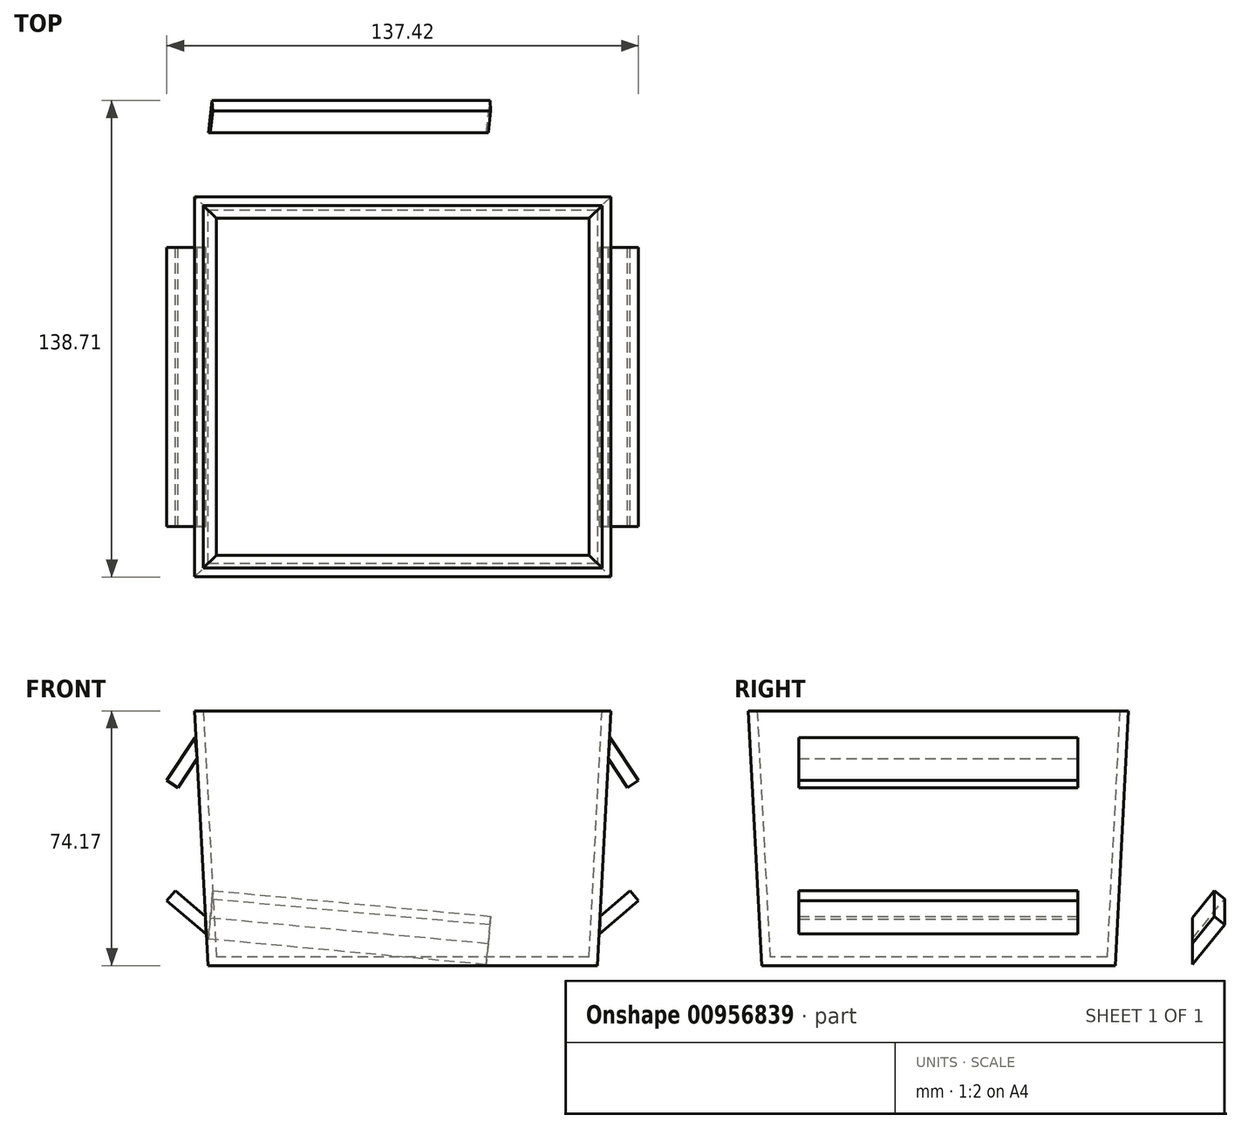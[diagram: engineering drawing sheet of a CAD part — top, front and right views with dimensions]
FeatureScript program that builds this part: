
annotation { "Feature Type Name" : "Feature", "Feature Type Description" : "" }
export const myFeature = defineFeature(function(context is Context, id is Id, definition is map)
    precondition{}
    {
        {
            var Q0;
            Q0=qCreatedBy(makeId("Top.planeOp"),FACE);
            var sketch = newSketch(context, id + "F0", { "sketchPlane" : qUnion([Q0])});
            skLineSegment(sketch, "E0.bottom", {"start": v(56.73, -51.48) * mm, "end": v(-56.73, -51.48) * mm});
            skLineSegment(sketch, "E0.top", {"start": v(56.73, 51.48) * mm, "end": v(-56.73, 51.48) * mm});
            skLineSegment(sketch, "E0.left", {"start": v(56.73, -51.48) * mm, "end": v(56.73, 51.48) * mm});
            skLineSegment(sketch, "E0.right", {"start": v(-56.73, -51.48) * mm, "end": v(-56.73, 51.48) * mm});
            skPoint(sketch, "E0.middle", {"position": v(0, 0) * mm});
            skSolve(sketch);
        }
        {
            var Q0;
            Q0 = qSketchRegion(id + "F0", true);
            extrude(context, id + "F1", {"entities" : qUnion([Q0]), "depth" : 74.17 * mm, "offsetDistance" : 25.4 * mm, "hasDraft" : true, "draftAngle" : 3 * degree});
        }
        {
            var Q0;
            Q0=makeQuery(id+"F1.opExtrude","CAP_FACE",FACE,{"disambiguationData":[OSD([sQuery(id+"F0.wireOp",EDGE,"E0.bottom"),sQuery(id+"F0.wireOp",EDGE,"E0.top"),sQuery(id+"F0.wireOp",EDGE,"E0.left"),sQuery(id+"F0.wireOp",EDGE,"E0.right")])],"isStart":false});
            shell(context, id + "F2", {"entities" : qUnion([Q0]), "thickness" : 2.54 * mm});
        }
        {
            var Q0;
            Q0=qCreatedBy(makeId("Front.planeOp"),FACE);
            var sketch = newSketch(context, id + "F3", { "sketchPlane" : qUnion([Q0])});
            skLineSegment(sketch, "E1", {"start": v(60.46, 66.31) * mm, "end": v(68.7, 53.89) * mm});
            skLineSegment(sketch, "E2", {"start": v(68.7, 53.89) * mm, "end": v(65.52, 51.77) * mm});
            skLineSegment(sketch, "E3", {"start": v(65.52, 51.77) * mm, "end": v(59.9, 60.23) * mm});
            skLineSegment(sketch, "E4", {"start": v(59.9, 60.23) * mm, "end": v(60.46, 66.31) * mm});
            skLineSegment(sketch, "E5", {"start": v(57.37, 9.22) * mm, "end": v(68.7, 18.93) * mm});
            skLineSegment(sketch, "E6", {"start": v(68.7, 18.93) * mm, "end": v(66.2, 21.84) * mm});
            skLineSegment(sketch, "E7", {"start": v(66.2, 21.84) * mm, "end": v(57.44, 14.33) * mm});
            skLineSegment(sketch, "E8", {"start": v(57.44, 14.33) * mm, "end": v(57.37, 9.22) * mm});
            skLineSegment(sketch, "E9", {"start": v(58.59, 37.27) * mm, "end": v(98.17, 35.2) * mm, "construction": true});
            skSolve(sketch);
        }
        {
            var Q0;
            Q0 = qSketchRegion(id + "F3", true);
            extrude(context, id + "F4", {"entities" : qUnion([Q0]), "operationType" : NewBodyOperationType.ADD, "endBound" : BoundingType.SYMMETRIC, "depth" : 81.28 * mm, "offsetDistance" : 25.4 * mm});
        }
        {
            var Q0;
            Q0=makeQuery(id+"F4.opExtrude","SWEPT_BODY",BODY,{"disambiguationData":[OSD([sQuery(id+"F3.wireOp",EDGE,"E1"),sQuery(id+"F3.wireOp",EDGE,"E2"),sQuery(id+"F3.wireOp",EDGE,"E3"),sQuery(id+"F3.wireOp",EDGE,"E4")])]});
            var Q1;
            Q1=makeQuery(id+"F1.opExtrude","SWEPT_BODY",BODY,{"disambiguationData":[OSD([sQuery(id+"F0.wireOp",EDGE,"E0.bottom"),sQuery(id+"F0.wireOp",EDGE,"E0.top"),sQuery(id+"F0.wireOp",EDGE,"E0.left"),sQuery(id+"F0.wireOp",EDGE,"E0.right")])]});
            var Q2;
            Q2=qCreatedBy(makeId("Right.planeOp"),FACE);
            mirror(context, id + "F5", {"operationType" : NewBodyOperationType.ADD, "entities" : qUnion([Q0, Q1]), "mirrorPlane" : qUnion([Q2])});
        }
        {
            var Q0;
            Q0=makeQuery(id+"F4.opExtrude","SWEPT_BODY",BODY,{"disambiguationData":[OSD([sQuery(id+"F3.wireOp",EDGE,"E1"),sQuery(id+"F3.wireOp",EDGE,"E2"),sQuery(id+"F3.wireOp",EDGE,"E3"),sQuery(id+"F3.wireOp",EDGE,"E4")])]});
            var Q1;
            Q1=makeQuery(id+"F1.opExtrude","CAP_EDGE",EDGE,{"disambiguationData":[OSD([sQuery(id+"F0.wireOp",EDGE,"E0.left")])],"isStart":false});
            transform(context, id + "F6", {"entities" : qUnion([Q0]), "transformType" : TransformType.TRANSLATION_ENTITY, "oppositeDirectionEntity" : false, "transformLine" : qUnion([Q1]), "makeCopy" : true});
        }
        {
            var Q0;
            Q0=makeQuery(id+"F6.opPattern","COPY",BODY,{"derivedFrom":makeQuery(id+"F4.opExtrude","SWEPT_BODY",BODY,{"disambiguationData":[OSD([sQuery(id+"F3.wireOp",EDGE,"E1"),sQuery(id+"F3.wireOp",EDGE,"E2"),sQuery(id+"F3.wireOp",EDGE,"E3"),sQuery(id+"F3.wireOp",EDGE,"E4")])]}),"instanceName":"1"});
            var Q1;
            Q1=makeQuery(id+"F6.opPattern","COPY",EDGE,{"derivedFrom":makeQuery(id+"F4.opExtrude","CAP_EDGE",EDGE,{"disambiguationData":[OSD([sQuery(id+"F3.wireOp",EDGE,"E4")])],"isStart":false}),"instanceName":"1"});
            transform(context, id + "F7", {"entities" : qUnion([Q0]), "transformType" : TransformType.ROTATION, "transformAxis" : qUnion([Q1]), "angle" : 90 * degree, "makeCopy" : false});
        }
        {
            var Q0;
            Q0=qCreatedBy(makeId("Top.planeOp"),FACE);
            var sketch = newSketch(context, id + "F8", { "sketchPlane" : qUnion([Q0])});
            skLineSegment(sketch, "E10", {"start": v(0, 0) * mm, "end": v(0, 120.94) * mm, "construction": true});
            skSolve(sketch);
        }
        {
            var Q0;
            Q0=makeQuery(id+"F6.opPattern","COPY",BODY,{"derivedFrom":makeQuery(id+"F4.opExtrude","SWEPT_BODY",BODY,{"disambiguationData":[OSD([sQuery(id+"F3.wireOp",EDGE,"E1"),sQuery(id+"F3.wireOp",EDGE,"E2"),sQuery(id+"F3.wireOp",EDGE,"E3"),sQuery(id+"F3.wireOp",EDGE,"E4")])]}),"instanceName":"1"});
            var Q1;
            Q1=sQuery(id+"F8.wireOp",EDGE,"E10");
            transform(context, id + "F9", {"entities" : qUnion([Q0]), "transformType" : TransformType.ROTATION, "transformAxis" : qUnion([Q1]), "angle" : 180 * degree, "makeCopy" : false});
        }
        {
            var Q0;
            Q0=makeQuery(id+"F6.opPattern","COPY",BODY,{"derivedFrom":makeQuery(id+"F4.opExtrude","SWEPT_BODY",BODY,{"disambiguationData":[OSD([sQuery(id+"F3.wireOp",EDGE,"E1"),sQuery(id+"F3.wireOp",EDGE,"E2"),sQuery(id+"F3.wireOp",EDGE,"E3"),sQuery(id+"F3.wireOp",EDGE,"E4")])]}),"instanceName":"1"});
            var Q1;
            Q1=makeQuery(id+"F1.opExtrude","SWEPT_EDGE",EDGE,{"disambiguationData":[OSD([sQuery(id+"F0.wireOp",EDGE,"E0.top"),sQuery(id+"F0.wireOp",EDGE,"E0.left")])]});
            transform(context, id + "F10", {"entities" : qUnion([Q0]), "transformType" : TransformType.TRANSLATION_ENTITY, "oppositeDirectionEntity" : true, "transformLine" : qUnion([Q1]), "makeCopy" : false});
        }
    });
